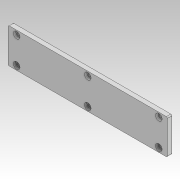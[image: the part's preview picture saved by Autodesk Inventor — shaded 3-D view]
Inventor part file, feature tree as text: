
AUTODESK INVENTOR PART (.ipt)
format: ipt  version: 2020 (Build 240168000, 168)  size: 124,416 bytes
history: native  units: mm
features: extrude x2, sketch x2
ambient origin geometry x8: Origin, YZ Plane, XZ Plane, XY Plane, X Axis, Y Axis, Z Axis, Center Point
bodies: Solid1 (feature_tree)
feature tree (4):
  extrude  "Extrusion1"  Depth=31.5mm
  extrude  "Extrusion2"  Depth=11.8875mm
  sketch  "Sketch1"  dims[d0=144.0mm d1=31.5mm]
  sketch  "Sketch2"  dims[d2=64.25mm d3=11.8875mm d4=3.5mm d5=1.0mm d6=4.0mm d7=0.0mm d8=6.0mm d9=2.2mm d10=0.0mm]
